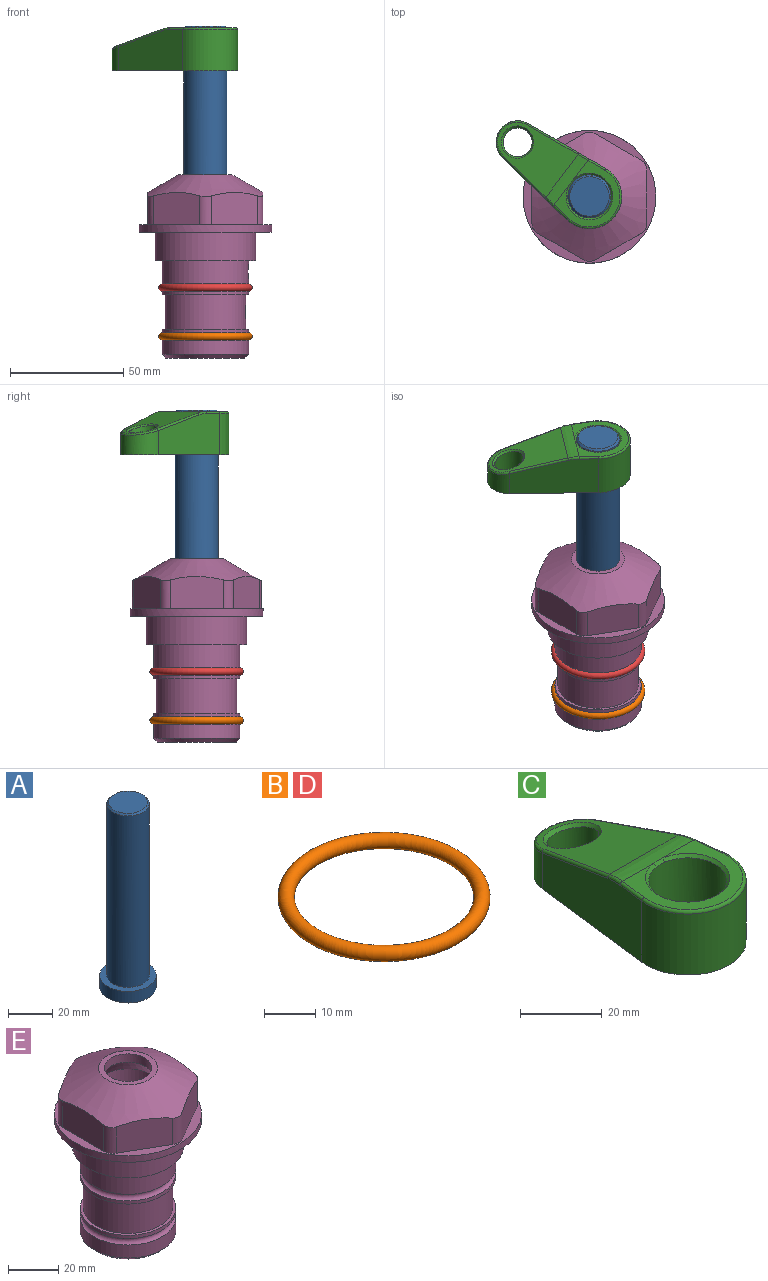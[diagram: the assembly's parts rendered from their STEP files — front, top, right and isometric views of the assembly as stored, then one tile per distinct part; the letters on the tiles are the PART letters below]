
ASSEMBLY  parts=5 mates=3
PART A: 6 faces, bbox 25.4x25.4x101.6 mm
  f0: plane 17.46x17.46mm, normal (0,0,1), area 239.5mm2, adj f5
  f1: plane 25.4x25.4mm, normal (0,0,-1), area 506.7mm2, adj f2
  f2: cylinder r=12.7mm len=25.4mm, axis (0,0,1), area 506.7mm2, adj f1,f3
  f3: plane 25.4x25.4mm, normal (0,0,1), area 221.7mm2, adj f2,f4
  f4: cylinder r=9.53mm len=94.46mm, axis (0,0,1), area 5653mm2, adj f3,f5
  f5: cone r=8.73mm half-angle=45deg, axis (0,0,-1), area 64.4mm2, adj f0,f4
PART B: 1 faces, bbox 44.7x44.7x3.2 mm
  f0: torus R=19.05mm, axis (0,0,1), area 1193.9mm2
PART C: 31 faces, bbox 31.7x65.5x19.8 mm
  f0: plane 39.12x18.26mm, normal (0.99,0.12,0), area 612.2mm2, adj f1,f4,f7,f11,f13,f15
  f1: cylinder r=9.53mm len=18.91mm, axis (0,0,-1), area 296.1mm2, adj f0,f2,f7,f17
  f2: plane 39.12x18.26mm, normal (-0.99,0.12,0), area 612.2mm2, adj f1,f4,f7,f12,f14,f16
  f3: cylinder r=6.35mm len=12.7mm, axis (0,0,-1), area 362.4mm2, adj f7,f18
  f4: cylinder r=14.29mm len=28.58mm, axis (0,0,-1), area 882.2mm2, adj f0,f2,f7,f10
  f5: cylinder r=9.53mm len=19.05mm, axis (0,0,-1), area 1092.6mm2, adj f7,f19,f20
  f6: plane 26.99x23.69mm, normal (0,0,1), area 216.2mm2, adj f9,f10,f11,f12,f19
  f7: plane 63.5x28.58mm, normal (0,0,-1), area 661.8mm2, adj f0,f1,f2,f3,f4,f5,f22,f23
  f8: plane 33.52x23.6mm, normal (0,0.26,0.97), area 486mm2, adj f9,f15,f16,f17,f18
  f9: cylinder r=19.05mm len=24.72mm, axis (1,0,0), area 120.4mm2, adj f6,f8,f13,f14,f20
  f10: torus R=13.49mm, axis (0,0,1), area 59mm2, adj f4,f6,f11,f12
  f11: cylinder r=0.79mm len=8.67mm, axis (0.12,-0.99,0), area 10.8mm2, adj f0,f6,f10,f13
  f12: cylinder r=0.79mm len=8.67mm, axis (0.12,0.99,0), area 10.8mm2, adj f2,f6,f10,f14
  f13: bspline ~4.95x1.42mm, area 6.1mm2, adj f0,f9,f11,f15
  f14: bspline ~4.95x1.42mm, area 6.1mm2, adj f2,f9,f12,f16
  f15: cylinder r=0.79mm len=25.95mm, axis (0.12,-0.96,0.26), area 32.9mm2, adj f0,f8,f13,f17
  f16: cylinder r=0.79mm len=25.95mm, axis (0.12,0.96,-0.26), area 32.9mm2, adj f2,f8,f14,f17
  f17: bspline ~18.91x8.38mm, area 30mm2, adj f1,f8,f15,f16
  f18: bspline ~14.29x14.29mm, area 48.3mm2, adj f3,f8
  f19: cone r=9.53mm half-angle=45deg, axis (0,0,1), area 66.5mm2, adj f5,f6,f20
  f20: bspline ~3.22x0.96mm, area 3.5mm2, adj f5,f9,f19
  f21: plane 2.75x2.72mm, normal (0,0,-1), area 2.9mm2, adj f23,f25,f28
  f22: plane 23.05x15.88mm, normal (-0.99,-0.12,0), area 323.6mm2, adj f7,f25,f26,f27,f28,f29
  f23: plane 23.05x15.88mm, normal (0.99,-0.12,0), area 323.6mm2, adj f7,f21,f25,f27,f28,f30
  f24: cylinder r=9.53mm len=10.69mm, axis (0,0,-1), area 114.7mm2, adj f7,f27,f29,f30
  f25: cylinder r=12.7mm len=20.59mm, axis (0,0,-1), area 381.1mm2, adj f7,f21,f22,f23,f26,f28
  f26: plane 2.75x2.72mm, normal (0,0,-1), area 2.9mm2, adj f22,f25,f28
  f27: plane 19.72x18.37mm, normal (0,-0.26,-0.97), area 291.8mm2, adj f22,f23,f24,f28,f29,f30
  f28: cylinder r=15.88mm len=19.92mm, axis (1,0,0), area 54.8mm2, adj f21,f22,f23,f25,f26,f27
  f29: cylinder r=1.59mm len=11mm, axis (0,0,-1), area 34.7mm2, adj f7,f22,f24,f27
  f30: cylinder r=1.59mm len=11mm, axis (0,0,-1), area 34.7mm2, adj f7,f23,f24,f27
PART D: same geometry as B
PART E: 36 faces, bbox 58.7x58.7x81 mm
  f0: cylinder r=17.78mm len=35.56mm, axis (0,0,1), area 1670.8mm2, adj f23,f24,f31
  f1: cylinder r=19.05mm len=38.1mm, axis (0,0,1), area 1191.9mm2, adj f26,f27,f30
  f2: plane 58.66x58.66mm, normal (0,0,-1), area 1150.6mm2, adj f3,f28
  f3: cylinder r=29.33mm len=58.66mm, axis (0,0,-1), area 585.1mm2, adj f2,f4
  f4: plane 58.66x58.66mm, normal (0,0,1), area 475.9mm2, adj f3,f5,f6,f7,f8,f9,f10,f11
  f5: plane 20.32x14.34mm, normal (-0.5,0.87,0), area 324.4mm2, adj f4,f15,f16,f17
  f6: plane 20.32x14.34mm, normal (0.5,0.87,0), area 324.4mm2, adj f4,f14,f15,f17
  f7: plane 23.48x14.34mm, normal (1,0,0), area 324.4mm2, adj f4,f13,f14,f17
  f8: plane 20.32x14.34mm, normal (0.5,-0.87,0), area 324.4mm2, adj f4,f12,f13,f17
  f9: plane 20.32x14.34mm, normal (-0.5,-0.87,0), area 324.4mm2, adj f4,f11,f12,f17
  f10: plane 23.48x14.34mm, normal (-1,0,0), area 324.4mm2, adj f4,f11,f16,f17
  f11: cylinder r=5.08mm len=12.85mm, axis (0,0,-1), area 67.2mm2, adj f4,f9,f10,f17
  f12: cylinder r=5.08mm len=12.85mm, axis (0,0,-1), area 67.2mm2, adj f4,f8,f9,f17
  f13: cylinder r=5.08mm len=12.85mm, axis (0,0,-1), area 67.2mm2, adj f4,f7,f8,f17
  f14: cylinder r=5.08mm len=12.85mm, axis (0,0,-1), area 67.2mm2, adj f4,f6,f7,f17
  f15: cylinder r=5.08mm len=12.85mm, axis (0,0,-1), area 67.2mm2, adj f4,f5,f6,f17
  f16: cylinder r=5.08mm len=12.85mm, axis (0,0,-1), area 67.2mm2, adj f4,f5,f10,f17
  f17: cone r=11.73mm half-angle=60deg, axis (0,0,-1), area 2071.8mm2, adj f5,f6,f7,f8,f9,f10,f11,f12
  f18: plane 23.46x23.46mm, normal (0,0,1), area 147.4mm2, adj f17,f35
  f19: plane 34.93x34.93mm, normal (0,0,-1), area 958mm2, adj f29
  f20: cylinder r=19.05mm len=38.1mm, axis (0,0,1), area 760.1mm2, adj f21,f29
  f21: torus R=19.05mm, axis (0,0,1), area 565.3mm2, adj f20,f22
  f22: cylinder r=19.05mm len=38.1mm, axis (0,0,1), area 190mm2, adj f21,f23
  f23: plane 38.1x38.1mm, normal (0,0,1), area 146.9mm2, adj f0,f22
  f24: plane 38.1x38.1mm, normal (0,0,-1), area 146.9mm2, adj f0,f25
  f25: cylinder r=19.05mm len=38.1mm, axis (0,0,1), area 190mm2, adj f24,f26
  f26: torus R=19.05mm, axis (0,0,1), area 565.3mm2, adj f1,f25
  f27: plane 44.45x44.45mm, normal (0,0,-1), area 411.7mm2, adj f1,f28
  f28: cylinder r=22.23mm len=44.45mm, axis (0,0,1), area 1773.5mm2, adj f2,f27
  f29: cone r=19.05mm half-angle=45deg, axis (0,0,1), area 257.5mm2, adj f19,f20
  f30: cylinder r=3.17mm len=6.75mm, axis (-1,0,0), area 128mm2, adj f1,f33
  f31: cylinder r=3.17mm len=6.35mm, axis (-1,0,0), area 102.5mm2, adj f0,f33
  f32: plane 25.4x25.4mm, normal (0,0,1), area 506.7mm2, adj f33
  f33: cylinder r=12.7mm len=66.42mm, axis (0,0,-1), area 5236.2mm2, adj f30,f31,f32,f34
  f34: cone r=9.53mm half-angle=30deg, axis (0,0,-1), area 443.4mm2, adj f33,f35
  f35: cylinder r=9.53mm len=19.05mm, axis (0,0,-1), area 240.9mm2, adj f18,f34
PLACE A rot(axis=(0,0,1),52.9deg) t=(0,0,27.55)mm
PLACE B t=(0,0,-21.59)mm
PLACE C rot(axis=(0,0,1),52.9deg) t=(0,0,26.76)mm
PLACE D at identity
PLACE E at identity fixed
MATE cylindrical A.f2 <-> E.f0  axis (0,0,-1) through (0,0,-10.55)mm
MATE fastened A.f2 <-> C.f4  axis (0,0,1) through (0,0,90.26)mm
MATE fastened D.f0 <-> E.f0  axis (0,0,1) through (0,0,-24.51)mm
